# Revit family: SDP-8615М_RV17_LOD400
name_source: partatom
category: Оборудование
revit_build: Autodesk Revit 2017 (Build: 20170118_1100(x64)
units: mm (PartAtom-declared; Revit-internal decimal feet)

## family parameters
Всегда вертикально = Нет
На основе рабочей плоскости = Нет
Общий = Нет
При загрузке вырезать с полостями = Нет
Размер круглого соединителя = Использовать диаметр
Тип детали = Нормальный
Точка расчета площади = Нет

## types (1)
- SDP-8615М тепловизор
    ADSK_URL страницы изделия = https://stilsoft.ru
    ADSK_Единица измерения = шт.
    ADSK_Завод-изготовитель = ООО «Основа Безопасности»
    ADSK_Количество = 1
    ADSK_Марка = СТВФ.426459.162
    ADSK_Масса = 10
    ADSK_Наименование = Тепловизор SDP-8615М
    ADSK_Размер_Глубина = 202 мм
    ADSK_Размер_Длина = 480 мм
    ADSK_Размер_Ширина = 210 мм
    d_короба = 0 мм
    Время непрерывной работы, не менее, ч = 2900
    Время установления рабочего режима, не более, мин = 5
    Детектор = Неохлаждаемая микроболометрическая матрица
    Интерфейс управления = 10BaseT/100BaseTХ Ethernet (RJ-45)
    Количество допустимых битых пикселей, до, % = 1
    Минимальное расстояние наблюдения, м = 50
    Минимальное фокусное расстояние, м = 1
    Мощность = 9.5
    Напряжение = 12
    Объектив = Моторизованный
    Оптика = Линза из кристаллического германия с просветляющими покрытиями
    Отклонение оттенков цвета от фактического значения,<unrecoverable-encoding: 5 bytes ef82b0d0a1> = ±1
    Поле зрения, <unrecoverable-encoding: 3 bytes ef82b0> = 13,7х10,3
    Пороговая чувствительность к перепаду температур,<unrecoverable-encoding: 5 bytes ef82b0d0a1> = 0.1
    Размер пикселей, мкм = 25
    Разрешение видеоизображения = 640х480
    Расстояние обнаружения цели типа «автомобиль», до, м = 7900 мм
    Расстояние обнаружения цели типа «человека», до, м = 4000 мм
    Расстояние распознавания цели типа  «автомобиль», до, м = 5300 мм
    Расстояние распознавания цели типа  «человека», до, м = 3000 мм
    Ресурс матрицы, ч = 25000
    Спектральный диапазон, мкм = 8-14
    Стандарт сжатия = H.264
    Управление режимами = Палитра (черно–белая, черно–белая инвертированная)
    Фокусное расстояние, мм = 150F1
    Частота кадров, Гц = 25
